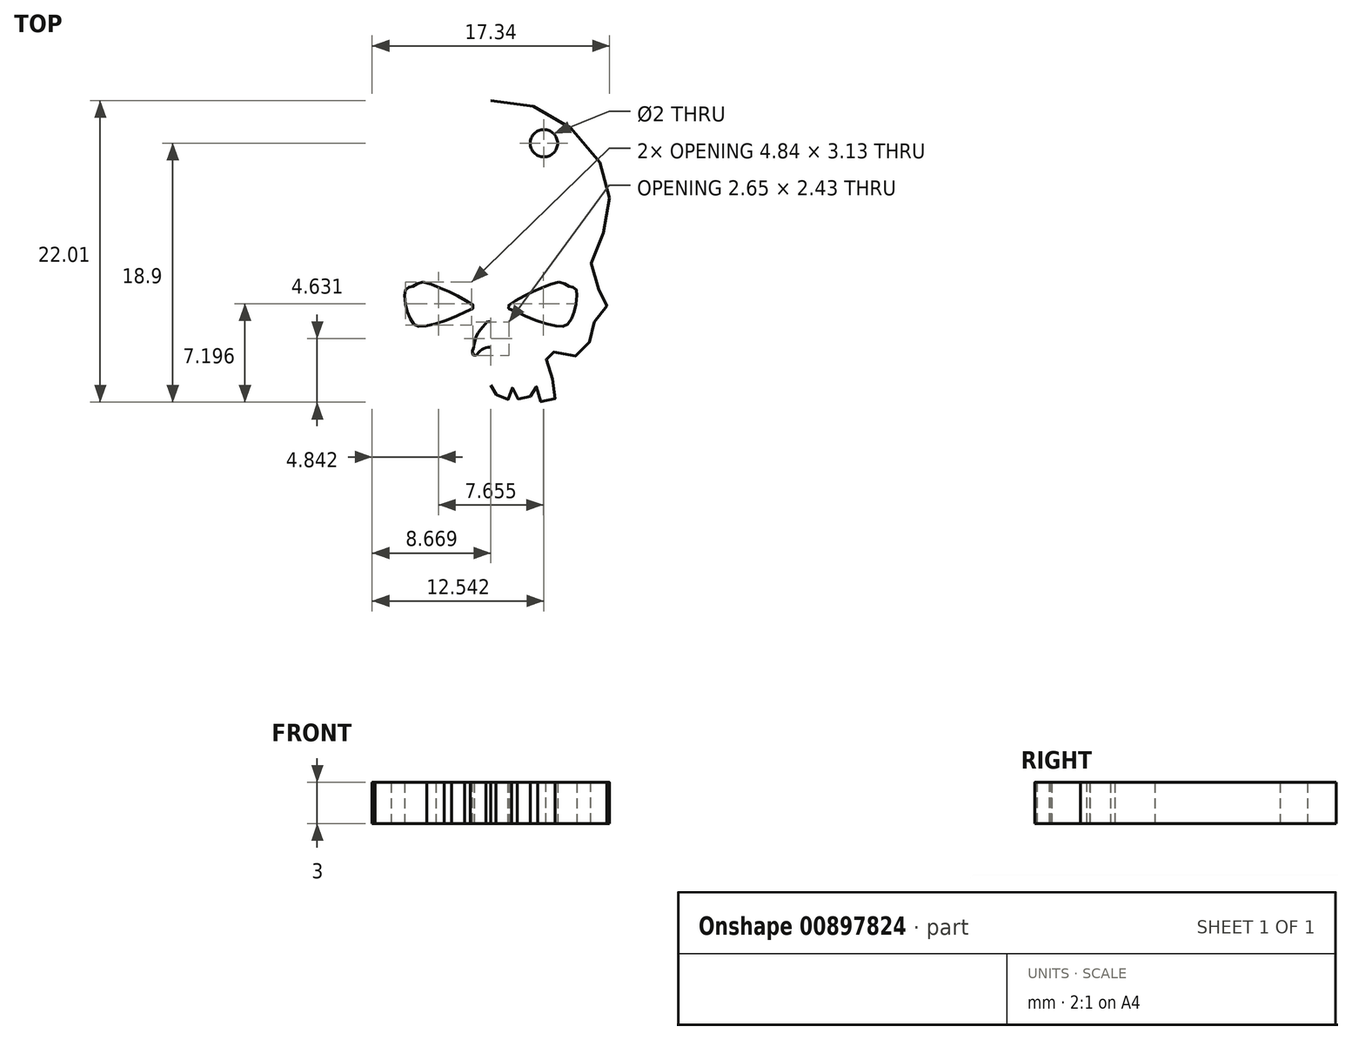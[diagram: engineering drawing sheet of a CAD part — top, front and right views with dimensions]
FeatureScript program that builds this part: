
annotation { "Feature Type Name" : "Feature", "Feature Type Description" : "" }
export const myFeature = defineFeature(function(context is Context, id is Id, definition is map)
    precondition{}
    {
        {
            var Q0;
            Q0=qCreatedBy(makeId("Top.planeOp"),FACE);
            var sketch = newSketch(context, id + "F0", { "sketchPlane" : qUnion([Q0])});
            skFitSpline(sketch, "E0", {"points": [v(-12.24, 23.5) * mm, v(-14.72, 23.26) * mm, v(-17.1, 22.26) * mm, v(-19.06, 20.48) * mm, v(-20.57, 18.25) * mm, v(-20.89, 16.54) * mm, v(-20.82, 15) * mm, v(-20.15, 13.13) * mm, v(-19.63, 11.84) * mm, v(-19.55, 10.97) * mm, v(-19.97, 9.93) * mm, v(-20.5, 9.34) * mm, v(-20.67, 8.88) * mm, v(-20.7, 8.54) * mm, v(-20.52, 8.07) * mm, v(-20.2, 7.7) * mm, v(-19.61, 7.14) * mm, v(-19.48, 6.7) * mm, v(-19.45, 5.95) * mm, v(-19.38, 5.58) * mm, v(-18.92, 5.1) * mm, v(-18.28, 4.83) * mm, v(-17.56, 4.87) * mm, v(-16.92, 5.12) * mm, v(-16.56, 5.28) * mm, v(-16.32, 5.28) * mm, v(-16.26, 4.9) * mm, v(-16.33, 4.33) * mm, v(-16.53, 3.83) * mm, v(-16.74, 3.19) * mm, v(-16.88, 2.47) * mm, v(-16.92, 2.04) * mm, v(-16.9, 1.69) * mm, v(-16.72, 1.52) * mm, v(-16.3, 1.5) * mm, v(-15.97, 1.5) * mm, v(-15.71, 1.65) * mm, v(-15.67, 2.16) * mm, v(-15.68, 2.52) * mm, v(-15.4, 2.68) * mm, v(-15.2, 2.64) * mm, v(-15.12, 2.4) * mm, v(-15.1, 1.9) * mm, v(-14.98, 1.67) * mm, v(-14.66, 1.64) * mm, v(-14.33, 1.64) * mm, v(-14.2, 1.81) * mm, v(-14.17, 2.24) * mm, v(-14.13, 2.52) * mm, v(-13.87, 2.56) * mm, v(-13.73, 2.47) * mm, v(-13.73, 2.13) * mm, v(-13.73, 1.91) * mm, v(-13.56, 1.71) * mm, v(-13.25, 1.68) * mm, v(-12.92, 1.7) * mm, v(-12.74, 1.8) * mm, v(-12.63, 2.09) * mm, v(-12.62, 2.42) * mm, v(-12.6, 2.61) * mm, v(-12.48, 2.72) * mm, v(-12.24, 2.74) * mm], "startDerivative": vector(-71.6, -2.86) * mm, "endDerivative": vector(23.24, -1.5) * mm});
            skFitSpline(sketch, "E1", {"points": [v(-17.21, 10.25) * mm, v(-17.66, 10.1) * mm, v(-17.95, 9.93) * mm, v(-18.18, 9.9) * mm, v(-18.43, 9.76) * mm, v(-18.53, 9.48) * mm, v(-18.45, 8.58) * mm, v(-18.24, 7.86) * mm, v(-17.9, 7.22) * mm, v(-17.56, 7.02) * mm, v(-16.8, 7.09) * mm, v(-15.15, 7.6) * mm, v(-13.86, 8.18) * mm, v(-13.46, 8.44) * mm, v(-13.84, 8.78) * mm, v(-14.95, 9.39) * mm, v(-16.09, 9.9) * mm, v(-17.21, 10.25) * mm]});
            skFitSpline(sketch, "E2", {"points": [v(-12.24, 7.34) * mm, v(-12.46, 7.38) * mm, v(-12.79, 7.05) * mm, v(-13.3, 6.32) * mm, v(-13.48, 5.59) * mm, v(-13.54, 5.39) * mm, v(-13.6, 5.1) * mm, v(-13.43, 4.9) * mm, v(-13.23, 5.01) * mm, v(-13.1, 5.17) * mm, v(-12.85, 5.36) * mm, v(-12.59, 5.47) * mm, v(-12.24, 5.51) * mm], "startDerivative": vector(-3.25, 1.43) * mm, "endDerivative": vector(5.89, -0.56) * mm});
            skFitSpline(sketch, "E3.MirrorC", {"points": [v(-7.27, 10.25) * mm, v(-6.82, 10.1) * mm, v(-6.53, 9.93) * mm, v(-6.3, 9.9) * mm, v(-6.05, 9.76) * mm, v(-5.96, 9.48) * mm, v(-6.03, 8.58) * mm, v(-6.24, 7.86) * mm, v(-6.6, 7.22) * mm, v(-6.92, 7.02) * mm, v(-7.67, 7.09) * mm, v(-9.33, 7.6) * mm, v(-10.62, 8.18) * mm, v(-11.03, 8.44) * mm, v(-10.64, 8.78) * mm, v(-9.53, 9.39) * mm, v(-8.4, 9.9) * mm, v(-7.27, 10.25) * mm]});
            skFitSpline(sketch, "E4.MirrorCS", {"points": [v(-12.24, 23.5) * mm, v(-9.76, 23.26) * mm, v(-7.38, 22.26) * mm, v(-5.42, 20.48) * mm, v(-3.91, 18.25) * mm, v(-3.6, 16.54) * mm, v(-3.67, 15) * mm, v(-4.33, 13.13) * mm, v(-4.85, 11.84) * mm, v(-4.93, 10.97) * mm, v(-4.5, 9.93) * mm, v(-3.99, 9.34) * mm, v(-3.81, 8.88) * mm, v(-3.79, 8.54) * mm, v(-3.96, 8.07) * mm, v(-4.27, 7.7) * mm, v(-4.87, 7.14) * mm, v(-5, 6.7) * mm, v(-5.03, 5.95) * mm, v(-5.1, 5.58) * mm, v(-5.56, 5.1) * mm, v(-6.2, 4.83) * mm, v(-6.92, 4.87) * mm, v(-7.57, 5.12) * mm, v(-7.93, 5.28) * mm, v(-8.16, 5.28) * mm, v(-8.22, 4.9) * mm, v(-8.15, 4.33) * mm, v(-7.95, 3.83) * mm, v(-7.74, 3.19) * mm, v(-7.6, 2.47) * mm, v(-7.57, 2.04) * mm, v(-7.58, 1.69) * mm, v(-7.76, 1.52) * mm, v(-8.17, 1.5) * mm, v(-8.5, 1.5) * mm, v(-8.77, 1.65) * mm, v(-8.8, 2.16) * mm, v(-8.8, 2.52) * mm, v(-9.07, 2.68) * mm, v(-9.29, 2.64) * mm, v(-9.36, 2.4) * mm, v(-9.37, 1.9) * mm, v(-9.5, 1.67) * mm, v(-9.82, 1.64) * mm, v(-10.15, 1.64) * mm, v(-10.3, 1.81) * mm, v(-10.3, 2.24) * mm, v(-10.35, 2.52) * mm, v(-10.61, 2.56) * mm, v(-10.76, 2.47) * mm, v(-10.75, 2.13) * mm, v(-10.76, 1.91) * mm, v(-10.92, 1.71) * mm, v(-11.24, 1.68) * mm, v(-11.56, 1.7) * mm, v(-11.75, 1.8) * mm, v(-11.85, 2.09) * mm, v(-11.87, 2.42) * mm, v(-11.88, 2.61) * mm, v(-12, 2.72) * mm, v(-12.24, 2.74) * mm], "startDerivative": vector(71.6, -2.86) * mm, "endDerivative": vector(-23.24, -1.5) * mm});
            skFitSpline(sketch, "E5.MirrorCS", {"points": [v(-12.24, 7.34) * mm, v(-12.03, 7.38) * mm, v(-11.7, 7.05) * mm, v(-11.18, 6.32) * mm, v(-11, 5.59) * mm, v(-10.94, 5.39) * mm, v(-10.9, 5.1) * mm, v(-11.05, 4.9) * mm, v(-11.26, 5.01) * mm, v(-11.4, 5.17) * mm, v(-11.63, 5.36) * mm, v(-11.9, 5.47) * mm, v(-12.24, 5.51) * mm], "startDerivative": vector(3.25, 1.43) * mm, "endDerivative": vector(-5.89, -0.56) * mm});
            skLineSegment(sketch, "E6.trimOffspring", {"start": v(-12.24, 23.5) * mm, "end": v(-12.24, 23.71) * mm});
            skCircle(sketch, "E7", {"center": v(-8.37, 20.4) * mm, "radius": 1 * mm});
            skSolve(sketch);
        }
        {
            var Q0;
            Q0=makeQuery(id+"F0.imprint","IMPRINT",FACE,{"disambiguationData":[TD([[makeQuery(id+"F0.imprint","IMPRINT",EDGE,{"derivedFrom":sQuery(id+"F0.wireOp",EDGE,"E0")}),1.0]])]});
            extrude(context, id + "F1", {"entities" : qUnion([Q0]), "depth" : 3 * mm, "offsetDistance" : 25 * mm});
        }
    });
